# Revit family: Cleanout_Floor_Adjustable-Zurn-Z1454-Flashing-flange
name_source: partatom
category: Plumbing Fixtures
units: mm (PartAtom-declared; Revit-internal decimal feet)

## family parameters
Always vertical = Yes
Cut with Voids When Loaded = No
Maintain Annotation Orientation = No
OmniClass Number = 23.70.50.21.24.14
OmniClass Title = Deck Waste Water Drains
Part Type = Normal
Room Calculation Point = No
Round Connector Dimension = Use Radius
Shared = No
Work Plane-Based = No

## types (12) — shared parameters
Assembly Code = D2030300
Body Diameter = 13.5 "
CW Connection = No
Default Elevation = 2 "
Description = ADJUSTABLE FLOOR CLEANOUT W/ FLASHING FLANGE
HW Connection = No
Main Material = Iron - Zurn - Cast - Painted - Blue
Manufacturer = Zurn Water, LLC
Manufacurer Brand = Zurn
Modified Date = 12/30/25
Product Documentation Link = https://files.zurn.com
Product Page URL = https://www.zurn.com
Product data url = https://www.bimobject.com
URL = www.zurn.com
Vent Connection = No
WFU = 1
Waste Connection = Yes
zero-valued in all types: CWFU, HWFU

## per-type parameters (varying)
| type | Approx. Weight (Lbs) | Body Height E | Connector Radius | Grate Material | Model | Pipe Size A | Pipe Size-A (Inner dia) | Pipe Size-A (Outer dia) | Type Comments | ZN-Top | ZN-Top value |
| Z1454-2IC | 33 " | 5.25 " | 1 " | Iron - Zurn - Cast - Painted - Blue | Z1454 | 2 " | 2.067 " | 2.375 " | Z1454-2 Inch Inside Caulk Outlet | No | 0 " |
| Z1454-3IC | 33 " | 5.25 " | 1.5 " | Iron - Zurn - Cast - Painted - Blue | Z1454 | 3 " | 3.068 " | 3.5 " | Z1454-3 Inch Inside Caulk Outlet | No | 0 " |
| Z1454-4IC | 34 " | 5.25 " | 2 " | Iron - Zurn - Cast - Painted - Blue | Z1454 | 4 " | 4.026 " | 4.5 " | Z1454-4 Inch Inside Caulk Outlet | No | 0 " |
| Z1454-2IP | 33 " | 4.25 " | 1 " | Iron - Zurn - Cast - Painted - Blue | Z1454 | 2 " | 2.067 " | 2.375 " | Z1454-2 Inch Threaded Outlet | No | 0 " |
| Z1454-3IP | 33 " | 4.25 " | 1.5 " | Iron - Zurn - Cast - Painted - Blue | Z1454 | 3 " | 3.068 " | 3.5 " | Z1454-3 Inch Threaded Outlet | No | 0 " |
| Z1454-4IP | 34 " | 4.25 " | 2 " | Iron - Zurn - Cast - Painted - Blue | Z1454 | 4 " | 4.026 " | 4.5 " | Z1454-4 Inch Threaded Outlet | No | 0 " |
| ZN1454-2IC | 33 " | 5.25 " | 1 " | Bronze - Zurn - Polished Nickel | ZN1454 | 2 " | 2.067 " | 2.375 " | ZN1454-2 Inch Inside Caulk Outlet | Yes | 0.188 " |
| ZN1454-3IC | 33 " | 5.25 " | 1.5 " | Bronze - Zurn - Polished Nickel | ZN1454 | 3 " | 3.068 " | 3.5 " | ZN1454-3 Inch Inside Caulk Outlet | Yes | 0.188 " |
| ZN1454-4IC | 34 " | 5.25 " | 2 " | Bronze - Zurn - Polished Nickel | ZN1454 | 4 " | 4.026 " | 4.5 " | ZN1454-4 Inch Inside Caulk Outlet | Yes | 0.188 " |
| ZN1454-2IP | 33 " | 4.25 " | 1 " | Bronze - Zurn - Polished Nickel | ZN1454 | 2 " | 2.067 " | 2.375 " | ZN1454-2 Inch Threaded Outlet | Yes | 0.188 " |
| ZN1454-3IP | 33 " | 4.25 " | 1.5 " | Bronze - Zurn - Polished Nickel | ZN1454 | 3 " | 3.068 " | 3.5 " | ZN1454-3 Inch Threaded Outlet | Yes | 0.188 " |
| ZN1454-4IP | 34 " | 4.25 " | 2 " | Bronze - Zurn - Polished Nickel | ZN1454 | 4 " | 4.026 " | 4.5 " | ZN1454-4 Inch Threaded Outlet | Yes | 0.188 " |

## geometry (parser evidence)
native form markers: Sweep x2
no freeform markers — native parametric forms only
